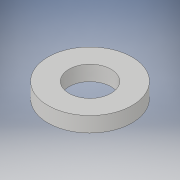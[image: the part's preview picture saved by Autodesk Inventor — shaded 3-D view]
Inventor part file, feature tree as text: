
AUTODESK INVENTOR PART (.ipt)
format: ipt  version: 2017 (Build 210142000, 142)  size: 96,256 bytes
history: native  units: in
note: dims shown in document units (in); Inventor stores cm internally (conversion verified against a paired STEP export)
features: extrude x1, sketch x1
ambient origin geometry x8: Origin, YZ Plane, XZ Plane, XY Plane, X Axis, Y Axis, Z Axis, Center Point
bodies: Solid1 (feature_tree)
feature tree (2):
  extrude  "Extrusion1"  Depth=0.09in
  sketch  "Sketch1"  dims[d0=0.25in d1=0.5in d2=0.09in d3=0.0in]
